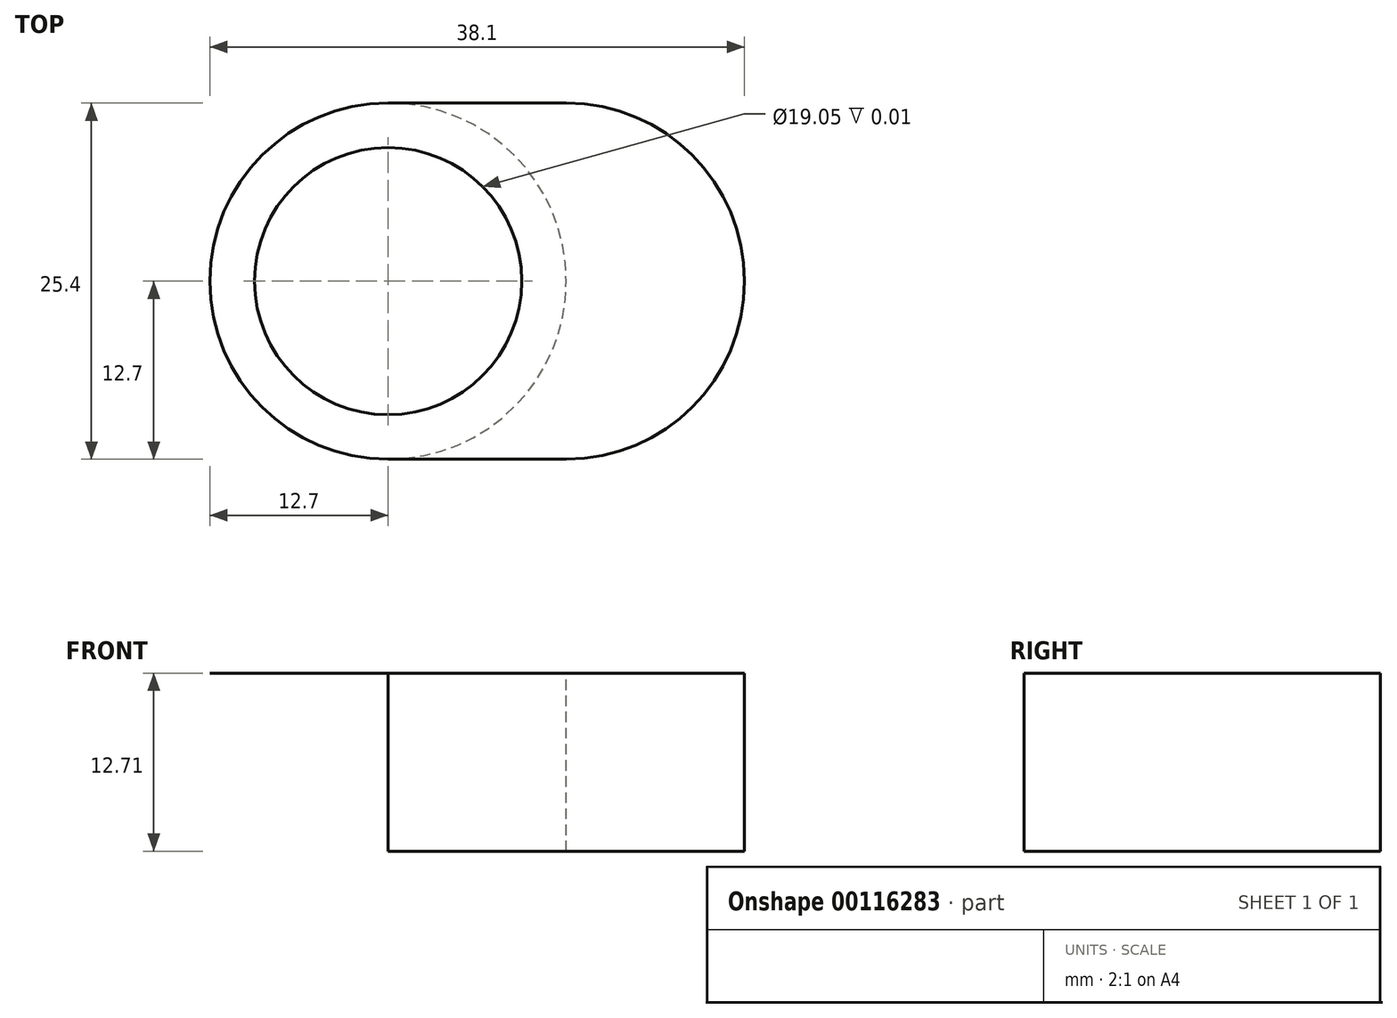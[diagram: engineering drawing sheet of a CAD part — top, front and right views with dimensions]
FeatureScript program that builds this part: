
annotation { "Feature Type Name" : "Feature", "Feature Type Description" : "" }
export const myFeature = defineFeature(function(context is Context, id is Id, definition is map)
    precondition{}
    {
        {
            var Q0;
            Q0=qCreatedBy(makeId("Top.planeOp"),FACE);
            var sketch = newSketch(context, id + "F0", { "sketchPlane" : qUnion([Q0])});
            skCircle(sketch, "E0", {"center": v(0, 0) * mm, "radius": 9.53 * mm});
            skArc(sketch, "E1", {"start": v(0, 12.7) * mm, "mid": v(-12.7, 0) * mm, "end": v(0, -12.7) * mm});
            skLineSegment(sketch, "E2", {"start": v(0, 0) * mm, "end": v(12.7, 0) * mm, "construction": true});
            skArc(sketch, "E3", {"start": v(12.7, -12.7) * mm, "mid": v(25.4, 0) * mm, "end": v(12.7, 12.7) * mm});
            skLineSegment(sketch, "E4", {"start": v(0, -12.7) * mm, "end": v(0, 12.7) * mm, "construction": true});
            skLineSegment(sketch, "E5", {"start": v(0, 12.7) * mm, "end": v(12.7, 12.7) * mm});
            skLineSegment(sketch, "E6", {"start": v(12.7, 12.7) * mm, "end": v(12.7, -12.7) * mm, "construction": true});
            skLineSegment(sketch, "E7", {"start": v(12.7, -12.7) * mm, "end": v(0, -12.7) * mm});
            skSolve(sketch);
        }
        {
            var Q0;
            Q0=makeQuery(id+"F0.imprint","IMPRINT",FACE,{"disambiguationData":[TD([[makeQuery(id+"F0.imprint","IMPRINT",EDGE,{"derivedFrom":sQuery(id+"F0.wireOp",EDGE,"E0")}),-1.0]])]});
            extrude(context, id + "F1", {"entities" : qUnion([Q0]), "depth" : 1 / 101.6 * mm});
        }
        {
            var Q0;
            Q0=makeQuery(id+"F1.opExtrude","CAP_FACE",FACE,{"disambiguationData":[OSD([sQuery(id+"F0.wireOp",EDGE,"E0"),sQuery(id+"F0.wireOp",EDGE,"E1"),sQuery(id+"F0.wireOp",EDGE,"E3"),sQuery(id+"F0.wireOp",EDGE,"E5"),sQuery(id+"F0.wireOp",EDGE,"E7")])],"isStart":true});
            var sketch = newSketch(context, id + "F2", { "sketchPlane" : qUnion([Q0])});
            skCircle(sketch, "E8", {"center": v(0, 0) * mm, "radius": 12.7 * mm});
            skCircle(sketch, "E9", {"center": v(0, 0) * mm, "radius": 9.53 * mm});
            skSolve(sketch);
        }
        {
            var Q0;
            {var subQ0=sQuery(id+"F2.wireOp",EDGE,"E8");Q0=makeQuery(id+"F2.imprint","IMPRINT",FACE,{"disambiguationData":[TD([[makeQuery(id+"F2.imprint","IMPRINT",EDGE,{"disambiguationData":[OD(0.0)],"derivedFrom":subQ0}),-1.0]])]});}
            extrude(context, id + "F3", {"entities" : qUnion([Q0]), "operationType" : NewBodyOperationType.ADD, "depth" : 12.7 * mm});
        }
    });
